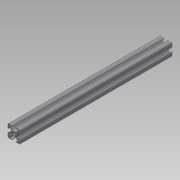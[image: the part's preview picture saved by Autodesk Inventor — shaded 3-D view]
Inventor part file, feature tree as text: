
AUTODESK INVENTOR PART (.ipt)
format: ipt  version: 2013 (Build 170138000, 138)  size: 205,824 bytes
history: native  units: in
note: dims shown in document units (in); Inventor stores cm internally (conversion verified against a paired STEP export)
features: extrude x1, sketch x1
ambient origin geometry x8: Origin, YZ Plane, XZ Plane, XY Plane, X Axis, Y Axis, Z Axis, Center Point
bodies: Solid1 (feature_tree)
feature tree (2):
  extrude  "Extrusion1"  [1 undecoded]
  sketch  "Sketch1"  dims[d0=12.0in d1=0.0in]
note: 1 required parameter value undecoded (feature->parameter linkage not recoverable at this tier; creation-order binding heuristic only, values carry confidence <= 0.55)
